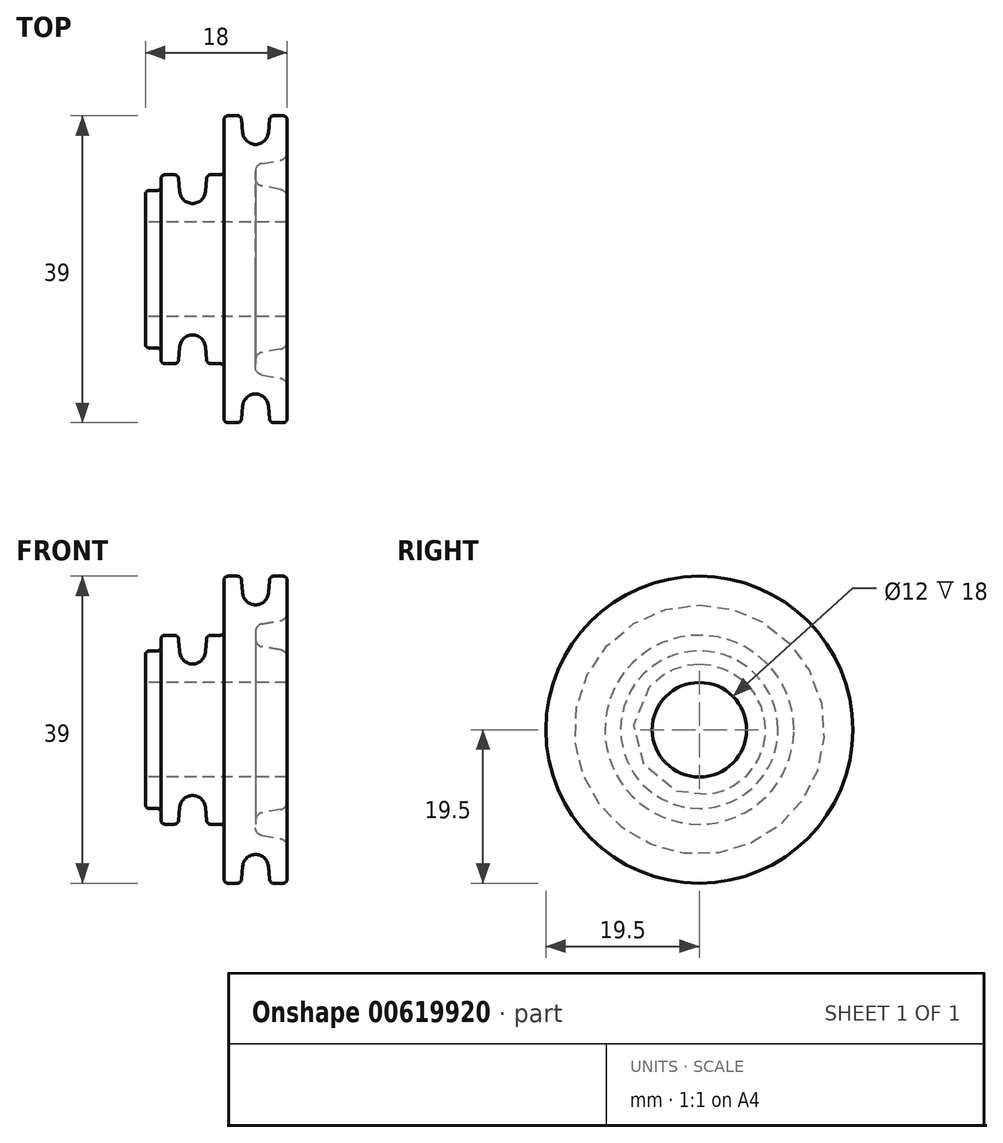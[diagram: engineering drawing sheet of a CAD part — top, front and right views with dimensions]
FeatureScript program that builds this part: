
annotation { "Feature Type Name" : "Feature", "Feature Type Description" : "" }
export const myFeature = defineFeature(function(context is Context, id is Id, definition is map)
    precondition{}
    {
        {
            var Q0;
            Q0=qCreatedBy(makeId("Front.planeOp"),FACE);
            var sketch = newSketch(context, id + "F0", { "sketchPlane" : qUnion([Q0])});
            skLineSegment(sketch, "E0", {"start": v(0, 0) * mm, "end": v(63.88, 0) * mm, "construction": true});
            skLineSegment(sketch, "E1", {"start": v(0, 6) * mm, "end": v(16, 6) * mm});
            skLineSegment(sketch, "E2", {"start": v(16, 6) * mm, "end": v(16, 9.16) * mm});
            skLineSegment(sketch, "E3", {"start": v(15.5, 19.5) * mm, "end": v(14.29, 19.5) * mm});
            skLineSegment(sketch, "E4", {"start": v(8, 19) * mm, "end": v(8, 12.5) * mm});
            skLineSegment(sketch, "E5", {"start": v(7.5, 12) * mm, "end": v(6.29, 12) * mm});
            skLineSegment(sketch, "E6", {"start": v(0, 11.5) * mm, "end": v(0, 10.5) * mm});
            skArc(sketch, "E7", {"start": v(10.36, 17.36) * mm, "mid": v(12, 15.85) * mm, "end": v(13.64, 17.36) * mm});
            skPoint(sketch, "E7.centerSnap0", {"position": v(12, 19.5) * mm});
            skArc(sketch, "E8", {"start": v(2.36, 9.86) * mm, "mid": v(4, 8.35) * mm, "end": v(5.64, 9.86) * mm});
            skPoint(sketch, "E8.centerSnap0", {"position": v(4, 12) * mm});
            skLineSegment(sketch, "E9", {"start": v(2.36, 9.86) * mm, "end": v(2.2, 11.54) * mm});
            skLineSegment(sketch, "E10", {"start": v(5.8, 11.54) * mm, "end": v(5.64, 9.86) * mm});
            skLineSegment(sketch, "E11", {"start": v(10.36, 17.36) * mm, "end": v(10.2, 19.04) * mm});
            skLineSegment(sketch, "E12", {"start": v(13.8, 19.04) * mm, "end": v(13.64, 17.36) * mm});
            skLineSegment(sketch, "E13.trimOffspring", {"start": v(1.71, 12) * mm, "end": v(0.5, 12) * mm});
            skLineSegment(sketch, "E14.trimOffspring", {"start": v(9.71, 19.5) * mm, "end": v(8.5, 19.5) * mm});
            skPoint(sketch, "E15.visualSharp", {"position": v(0, 12) * mm});
            skArc(sketch, "E15.filletArc", {"start": v(0.5, 12) * mm, "mid": v(0.15, 11.85) * mm, "end": v(0, 11.5) * mm});
            skPoint(sketch, "E16.visualSharp", {"position": v(2.17, 12) * mm});
            skArc(sketch, "E16.filletArc", {"start": v(2.2, 11.54) * mm, "mid": v(2.05, 11.87) * mm, "end": v(1.71, 12) * mm});
            skPoint(sketch, "E17.visualSharp", {"position": v(5.83, 12) * mm});
            skArc(sketch, "E17.filletArc", {"start": v(6.29, 12) * mm, "mid": v(5.95, 11.87) * mm, "end": v(5.8, 11.54) * mm});
            skPoint(sketch, "E18.visualSharp", {"position": v(8, 12) * mm});
            skArc(sketch, "E18.filletArc", {"start": v(7.5, 12) * mm, "mid": v(7.85, 12.15) * mm, "end": v(8, 12.5) * mm});
            skPoint(sketch, "E19.visualSharp", {"position": v(10.17, 19.5) * mm});
            skArc(sketch, "E19.filletArc", {"start": v(10.2, 19.04) * mm, "mid": v(10.05, 19.37) * mm, "end": v(9.71, 19.5) * mm});
            skPoint(sketch, "E20.visualSharp", {"position": v(8, 19.5) * mm});
            skArc(sketch, "E20.filletArc", {"start": v(8.5, 19.5) * mm, "mid": v(8.15, 19.35) * mm, "end": v(8, 19) * mm});
            skPoint(sketch, "E21.visualSharp", {"position": v(16, 19.5) * mm});
            skArc(sketch, "E21.filletArc", {"start": v(16, 19) * mm, "mid": v(15.85, 19.35) * mm, "end": v(15.5, 19.5) * mm});
            skPoint(sketch, "E22.visualSharp", {"position": v(13.83, 19.5) * mm});
            skArc(sketch, "E22.filletArc", {"start": v(14.29, 19.5) * mm, "mid": v(13.95, 19.37) * mm, "end": v(13.8, 19.04) * mm});
            skLineSegment(sketch, "E23.bottom", {"start": v(0, 6) * mm, "end": v(-2, 6) * mm});
            skLineSegment(sketch, "E23.top", {"start": v(-0.5, 10) * mm, "end": v(-1.5, 10) * mm});
            skLineSegment(sketch, "E23.left", {"start": v(0, 6) * mm, "end": v(0, 10) * mm});
            skLineSegment(sketch, "E23.right", {"start": v(-2, 6) * mm, "end": v(-2, 9.5) * mm});
            skLineSegment(sketch, "E24.right", {"start": v(12, 12.46) * mm, "end": v(12, 11.54) * mm});
            skLineSegment(sketch, "E25", {"start": v(12.83, 13.44) * mm, "end": v(15.17, 13.85) * mm});
            skLineSegment(sketch, "E26", {"start": v(15.17, 10.15) * mm, "end": v(12.83, 10.56) * mm});
            skLineSegment(sketch, "E27.trimOffspring", {"start": v(16, 14.84) * mm, "end": v(16, 19) * mm});
            skPoint(sketch, "E28.visualSharp", {"position": v(16, 14) * mm});
            skArc(sketch, "E28.filletArc", {"start": v(15.17, 13.85) * mm, "mid": v(15.77, 14.2) * mm, "end": v(16, 14.84) * mm});
            skPoint(sketch, "E29.visualSharp", {"position": v(16, 10) * mm});
            skArc(sketch, "E29.filletArc", {"start": v(16, 9.16) * mm, "mid": v(15.77, 9.8) * mm, "end": v(15.17, 10.15) * mm});
            skPoint(sketch, "E30.visualSharp", {"position": v(12, 10.7) * mm});
            skArc(sketch, "E30.filletArc", {"start": v(12, 11.54) * mm, "mid": v(12.23, 10.9) * mm, "end": v(12.83, 10.56) * mm});
            skPoint(sketch, "E31.visualSharp", {"position": v(12, 13.3) * mm});
            skArc(sketch, "E31.filletArc", {"start": v(12.83, 13.44) * mm, "mid": v(12.23, 13.1) * mm, "end": v(12, 12.46) * mm});
            skArc(sketch, "E32.filletArc", {"start": v(-0.5, 10) * mm, "mid": v(-0.15, 10.15) * mm, "end": v(0, 10.5) * mm});
            skPoint(sketch, "E33.visualSharp", {"position": v(-2, 10) * mm});
            skArc(sketch, "E33.filletArc", {"start": v(-1.5, 10) * mm, "mid": v(-1.85, 9.85) * mm, "end": v(-2, 9.5) * mm});
            skSolve(sketch);
        }
        {
            var Q0;
            Q0 = qSketchRegion(id + "F0", true);
            var Q1;
            Q1=sQuery(id+"F0.wireOp",EDGE,"E0");
            revolve(context, id + "F1", {"entities" : qUnion([Q0]), "axis" : qUnion([Q1]), "revolveType" : RevolveType.FULL});
        }
    });
